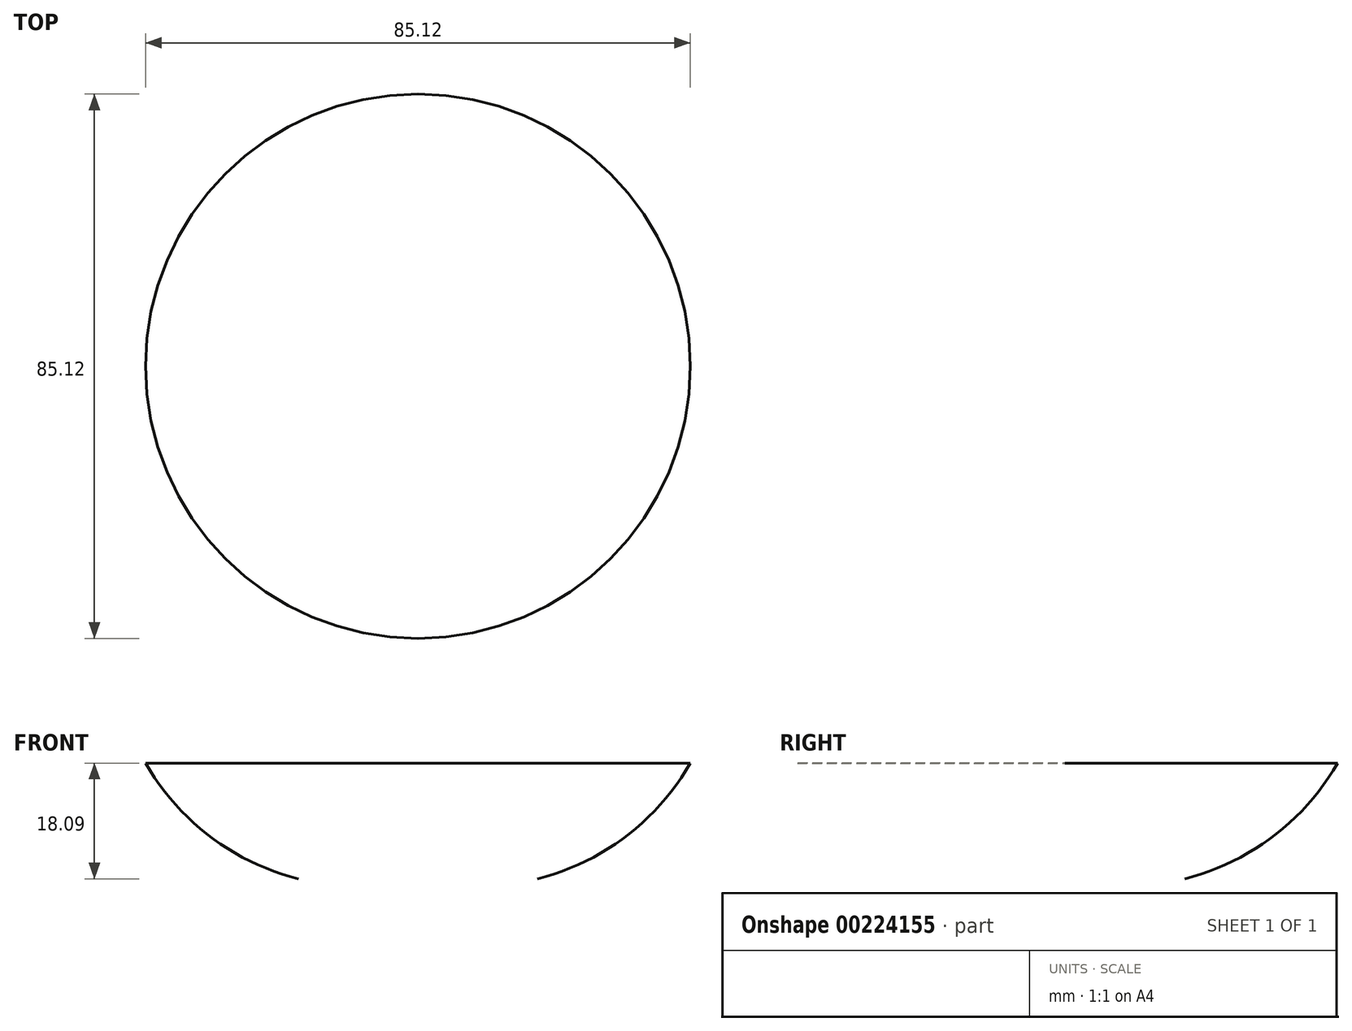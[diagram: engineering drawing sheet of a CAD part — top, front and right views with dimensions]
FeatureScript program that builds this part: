
annotation { "Feature Type Name" : "Feature", "Feature Type Description" : "" }
export const myFeature = defineFeature(function(context is Context, id is Id, definition is map)
    precondition{}
    {
        {
            var Q0;
            Q0=qCreatedBy(makeId("Front.planeOp"),FACE);
            var sketch = newSketch(context, id + "F0", { "sketchPlane" : qUnion([Q0])});
            skLineSegment(sketch, "E0", {"start": v(0, 56.1) * mm, "end": v(0, -56.4) * mm});
            skLineSegment(sketch, "E1", {"start": v(-44.3, 0) * mm, "end": v(42.56, 0) * mm});
            skArc(sketch, "E2", {"start": v(42.56, 0) * mm, "mid": v(39.83, 42.13) * mm, "end": v(0, 56.1) * mm});
            skSolve(sketch);
        }
        {
            var Q0;
            {var subQ0=sQuery(id+"F0.wireOp",EDGE,"E2");Q0=makeQuery(id+"F0.imprint","IMPRINT",FACE,{"disambiguationData":[TD([[makeQuery(id+"F0.imprint","IMPRINT",EDGE,{"derivedFrom":subQ0}),1.0]])]});}
            var Q1;
            Q1=sQuery(id+"F0.wireOp",EDGE,"E0");
            revolve(context, id + "F1", {"entities" : qUnion([Q0]), "axis" : qUnion([Q1]), "revolveType" : RevolveType.FULL});
        }
    });
